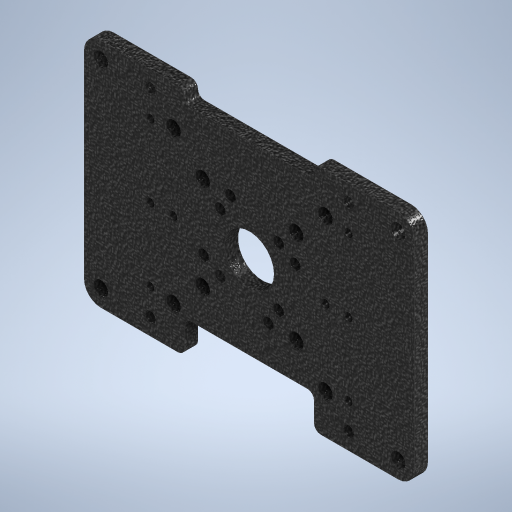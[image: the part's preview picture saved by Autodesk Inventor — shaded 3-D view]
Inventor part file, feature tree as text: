
AUTODESK INVENTOR PART (.ipt)
format: ipt  version: 2023 (Build 270158000, 158)  size: 477,696 bytes
history: native  units: mm
features: extrude x2, sketch x2, fillet x1
ambient origin geometry x8: Origin, YZ Plane, XZ Plane, XY Plane, X Axis, Y Axis, Z Axis, Center Point
bodies: Solid1 (feature_tree)
feature tree (5):
  extrude  "Extrusion1"  Depth=100.0mm
  extrude  "Extrusion2"  Depth=2.0mm
  fillet  "Fillet1"  Radius=50.0mm
  sketch  "Sketch1"  dims[d0=70.0mm d1=100.0mm]
  sketch  "Sketch2"  dims[d2=5.0mm d3=35.0mm d4=50.0mm d5=15.0mm d6=25.0mm d7=30.0mm d8=40.0mm d9=65.0mm d10=45.0deg d11=4.5mm d12=4.5mm d13=3.4mm d14=22.5deg d15=3.4mm d16=40.0mm d18=360.0deg d20=4.5mm d21=4.5mm d22=4.5mm d23=4.5mm d24=5.0mm d25=4.0mm d26=0.0mm d27=20.0mm d28=26.988mm d29=4.0mm d30=10.0mm d31=30.4mm d32=2.5mm d33=2.5mm d34=5.0mm d35=5.0mm d36=13.0mm d37=13.0mm d38=3.3mm d39=3.3mm d40=2.5mm d41=2.5mm d42=0.0mm d43=0.0mm d44=2.0mm]
